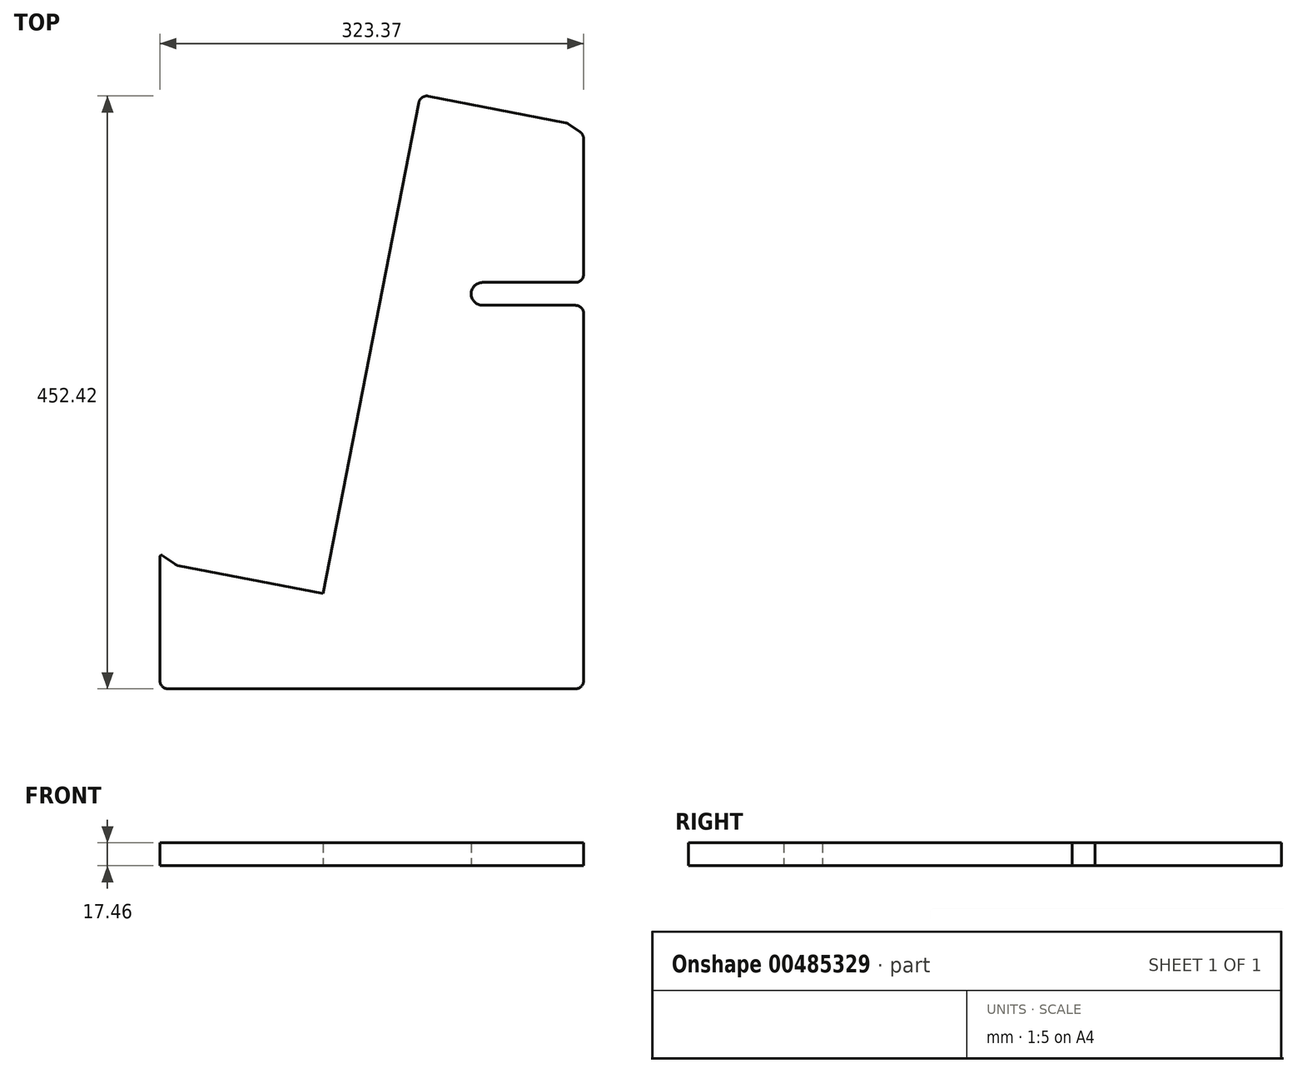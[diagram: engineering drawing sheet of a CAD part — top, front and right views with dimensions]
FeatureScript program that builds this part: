
annotation { "Feature Type Name" : "Feature", "Feature Type Description" : "" }
export const myFeature = defineFeature(function(context is Context, id is Id, definition is map)
    precondition{}
    {
        {
            var Q0;
            Q0=qCreatedBy(makeId("Top.planeOp"),FACE);
            var sketch = newSketch(context, id + "F0", { "sketchPlane" : qUnion([Q0])});
            skLineSegment(sketch, "E0", {"start": v(-95.53, 76.65) * mm, "end": v(-95.53, -96.88) * mm, "construction": true});
            skLineSegment(sketch, "E1", {"start": v(-95.53, -96.88) * mm, "end": v(232.75, -96.88) * mm, "construction": true});
            skLineSegment(sketch, "E2", {"start": v(-95.53, 0) * mm, "end": v(131.9, -44.2) * mm, "construction": true});
            skPoint(sketch, "E3", {"position": v(29.14, -24.23) * mm});
            skLineSegment(sketch, "E4", {"start": v(29.14, -24.23) * mm, "end": v(177.2, 737.5) * mm, "construction": true});
            skPoint(sketch, "E5", {"position": v(-83.06, -2.42) * mm});
            skPoint(sketch, "E6", {"position": v(-95.53, 6.35) * mm});
            skLineSegment(sketch, "E7", {"start": v(50.97, 195.8) * mm, "end": v(77.15, 195.8) * mm, "construction": true});
            skLineSegment(sketch, "E8", {"start": v(55.86, 213.27) * mm, "end": v(83, 213.27) * mm, "construction": true});
            skPoint(sketch, "E9", {"position": v(71.91, 195.8) * mm});
            skPoint(sketch, "E10", {"position": v(75.3, 213.27) * mm});
            skPoint(sketch, "E11", {"position": v(103.17, 356.63) * mm});
            skLineSegment(sketch, "E12", {"start": v(103.17, 356.63) * mm, "end": v(227.84, 332.4) * mm, "construction": true});
            skLineSegment(sketch, "E13", {"start": v(227.84, 332.4) * mm, "end": v(227.84, 219.62) * mm, "construction": true});
            skLineSegment(sketch, "E14", {"start": v(241.78, 204.54) * mm, "end": v(61.61, 204.54) * mm, "construction": true});
            skPoint(sketch, "E15", {"position": v(73.6, 204.54) * mm});
            skPoint(sketch, "E16", {"position": v(227.84, 204.54) * mm});
            skPoint(sketch, "E17", {"position": v(150.73, 204.54) * mm});
            skLineSegment(sketch, "E18", {"start": v(-93.53, 4.94) * mm, "end": v(-84.17, -1.64) * mm});
            skLineSegment(sketch, "E19", {"start": v(-95.53, 3.9) * mm, "end": v(-95.53, -90.53) * mm});
            skLineSegment(sketch, "E20", {"start": v(-81.73, -2.68) * mm, "end": v(29.14, -24.23) * mm});
            skLineSegment(sketch, "E21", {"start": v(70.91, 190.67) * mm, "end": v(29.14, -24.23) * mm});
            skPoint(sketch, "E22", {"position": v(227.84, 326.05) * mm});
            skPoint(sketch, "E23", {"position": v(215.37, 334.82) * mm});
            skLineSegment(sketch, "E24", {"start": v(225.14, 327.95) * mm, "end": v(216.48, 334.04) * mm});
            skLineSegment(sketch, "E25", {"start": v(214.04, 335.08) * mm, "end": v(109.4, 355.42) * mm});
            skLineSegment(sketch, "E26", {"start": v(101.96, 350.4) * mm, "end": v(76.78, 220.83) * mm});
            skLineSegment(sketch, "E27", {"start": v(227.84, 322.75) * mm, "end": v(227.84, 219.62) * mm});
            skLineSegment(sketch, "E28", {"start": v(-89.18, -96.88) * mm, "end": v(221.49, -96.88) * mm});
            skArc(sketch, "E29.filletArc", {"start": v(109.4, 355.42) * mm, "mid": v(104.64, 354.45) * mm, "end": v(101.96, 350.4) * mm});
            skArc(sketch, "E30.filletArc", {"start": v(216.48, 334.04) * mm, "mid": v(215.32, 334.7) * mm, "end": v(214.04, 335.08) * mm});
            skArc(sketch, "E31.filletArc", {"start": v(227.84, 322.75) * mm, "mid": v(227.13, 325.68) * mm, "end": v(225.14, 327.95) * mm});
            skPoint(sketch, "E32.visualSharp", {"position": v(227.84, -96.88) * mm});
            skArc(sketch, "E32.filletArc", {"start": v(221.49, -96.88) * mm, "mid": v(225.98, -95.02) * mm, "end": v(227.84, -90.53) * mm});
            skPoint(sketch, "E33.visualSharp", {"position": v(-95.53, -96.88) * mm});
            skArc(sketch, "E33.filletArc", {"start": v(-95.53, -90.53) * mm, "mid": v(-93.67, -95.02) * mm, "end": v(-89.18, -96.88) * mm});
            skArc(sketch, "E34.filletArc", {"start": v(-93.53, 4.94) * mm, "mid": v(-94.84, 5.03) * mm, "end": v(-95.53, 3.9) * mm});
            skArc(sketch, "E35.filletArc", {"start": v(-84.17, -1.64) * mm, "mid": v(-83, -2.3) * mm, "end": v(-81.73, -2.68) * mm});
            skLineSegment(sketch, "E36", {"start": v(75.3, 213.27) * mm, "end": v(71.91, 195.8) * mm});
            skLineSegment(sketch, "E37", {"start": v(150.73, 213.27) * mm, "end": v(221.49, 213.27) * mm});
            skLineSegment(sketch, "E38", {"start": v(150.73, 195.8) * mm, "end": v(221.49, 195.8) * mm});
            skArc(sketch, "E39", {"start": v(150.73, 213.27) * mm, "mid": v(142, 204.54) * mm, "end": v(150.73, 195.8) * mm});
            skLineSegment(sketch, "E40.trimOffspring", {"start": v(150.73, 213.27) * mm, "end": v(221.49, 213.27) * mm, "construction": true});
            skLineSegment(sketch, "E41.trimOffspring", {"start": v(150.73, 195.8) * mm, "end": v(221.49, 195.8) * mm, "construction": true});
            skLineSegment(sketch, "E42.trimOffspring", {"start": v(227.84, 189.45) * mm, "end": v(227.84, -191.89) * mm, "construction": true});
            skLineSegment(sketch, "E43.trimOffspring", {"start": v(227.84, 189.45) * mm, "end": v(227.84, -90.53) * mm});
            skLineSegment(sketch, "E44", {"start": v(76.78, 220.83) * mm, "end": v(75.3, 213.27) * mm});
            skLineSegment(sketch, "E45", {"start": v(71.91, 195.8) * mm, "end": v(70.91, 190.67) * mm});
            skPoint(sketch, "E46.visualSharp", {"position": v(227.84, 213.27) * mm});
            skArc(sketch, "E46.filletArc", {"start": v(221.49, 213.27) * mm, "mid": v(225.98, 215.13) * mm, "end": v(227.84, 219.62) * mm, "construction": true});
            skArc(sketch, "E47.filletArc", {"start": v(221.49, 213.27) * mm, "mid": v(225.98, 215.13) * mm, "end": v(227.84, 219.62) * mm});
            skPoint(sketch, "E48.visualSharp", {"position": v(227.84, 195.8) * mm});
            skArc(sketch, "E48.filletArc", {"start": v(227.84, 189.45) * mm, "mid": v(225.98, 193.94) * mm, "end": v(221.49, 195.8) * mm, "construction": true});
            skArc(sketch, "E49.filletArc", {"start": v(227.84, 189.45) * mm, "mid": v(225.98, 193.94) * mm, "end": v(221.49, 195.8) * mm});
            skSolve(sketch);
        }
        {
            var Q0;
            Q0 = qSketchRegion(id + "F0", true);
            extrude(context, id + "F1", {"entities" : qUnion([Q0]), "depth" : 17.46 * mm});
        }
    });
